# Revit family: FAP42TC
name_source: partatom
category: Communication Devices
revit_build: Autodesk Revit 2014 (Build: 20140709_2115(x64)
units: mm (PartAtom-declared; Revit-internal decimal feet)

## types (1)
- Two Way, Full Range, Coaxial Ceiling Loudspeaker
    100V Taps = 1, 2, 4, 8, and 16 Watts  & 8Q Bypass. Primary taps (@70.7V)
    70V Taps = 1, 2, 4, 8, and 16 Watts  & 8Ω
    Baffle Material = <By Category>
    Body Material = QF_Metal - Stainless - Polished
    Color = <By Category>
    Controls = Front Mounted Tap Selector Switch.
    Cost = 116.99 $
    Cost MSRP = 116.99 $
    Coverage Horizontal = 110.00°
    Coverage Vertical = 110.00°
    Depth = 10.5 "
    Description = 4" SHALLOW MOUNT COAXIAL IN-CEILING LOUDSPEAKER WITH 16-WATT 70/100V TRANSFORMER AND PORTED ENCLOSURE
    Dispersion Angle = 130.00°
    Enclosure Material = QF_Wall Paint-Gray
    Family Code (default) = LOUD SPEAKERS
    Frequency Response  = 83Hz – 20kHz (±7dB)
    Grill Material = QF_Plastic - Black - Fine Textured
    HF Driver = Coaxially Mounted PEI Dome Tweeter
    Height = 4.25 "
    IQ Category = SPEAKERS
    Impedance = 8
    Ingress Protection = IP-21
    Manufacturer = ATLAS SOUND
    Manufacturer URL = https://www.atlasied.com
    Market = Commercial, Higher Education, Emergency
    MasterFormat = 27 41 13
    MaterFormat Title = SPEAKERS
    Model = FAP42TC
    Mount Material = QF_Plastic - White - Smooth
    Mounting/Rigging Provisions = Patented Safety First Mounting System
    OmniClass Number = 23-37 17 13 19
    OmniClass Title = SPEAKERS
    Power Handling = 25
    Power Rating (RMS) = 25 Watts
    Product Documentation Link = https://www.atlasied.com
    Product Page URL = https://www.atlasied.com
    Regulatory Compliance = UL Listed to Comply with UL1480, UL2043 and CSA60065. Suitable for Use in Air Handling Spaces per NFPA 70 and NFPA 90
    SPL Max = 107
    Safety Agency Ratings = UL Listed to Comply with UL1480, UL2043 and CSA60065. Suitable for Use in Air Handling Spaces per NFPA 70 and NFPA 90
    Safety Features = 1 Safety Hang Point
    ScheduleType |RF| = AtlasIED Master
    Sensitivity = 88
    Speaker Dispersion = 130.00°
    Speaker Type = S1
    Transformer Option = Yes
    URL = www.atlassound.com
    Vertical Symmetry = Yes
    Warranty = 5 Year
    Weight Product = 6
    Width = 10.5 "

## geometry (parser evidence)
native form markers: Blend x6, Sweep x2
no freeform markers — native parametric forms only
